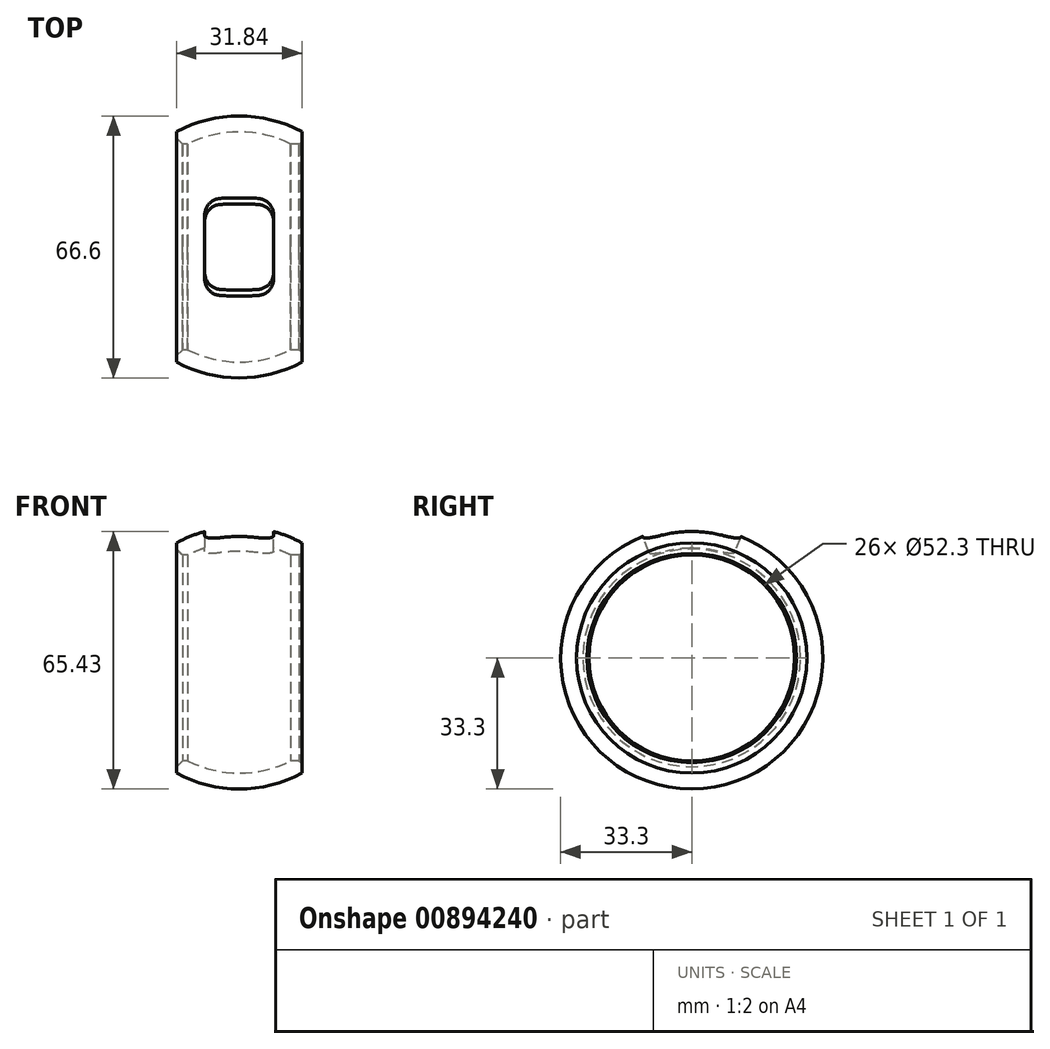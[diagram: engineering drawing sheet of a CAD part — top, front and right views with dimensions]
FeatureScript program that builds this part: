
annotation { "Feature Type Name" : "Feature", "Feature Type Description" : "" }
export const myFeature = defineFeature(function(context is Context, id is Id, definition is map)
    precondition{}
    {
        {
            var Q0;
            Q0=qCreatedBy(makeId("Front.planeOp"),FACE);
            var sketch = newSketch(context, id + "F0", { "sketchPlane" : qUnion([Q0])});
            skLineSegment(sketch, "E0", {"start": v(-15.92, 27.65) * mm, "end": v(-15.92, 29.25) * mm});
            skArc(sketch, "E1", {"start": v(15.92, 29.25) * mm, "mid": v(0, 33.3) * mm, "end": v(-15.92, 29.25) * mm});
            skLineSegment(sketch, "E2", {"start": v(15.22, 26.15) * mm, "end": v(13.07, 26.15) * mm});
            skLineSegment(sketch, "E3", {"start": v(-15.92, 27.65) * mm, "end": v(-14.42, 26.15) * mm});
            skLineSegment(sketch, "E4", {"start": v(-14.42, 26.15) * mm, "end": v(-13.07, 26.15) * mm});
            skLineSegment(sketch, "E5", {"start": v(15.92, 29.25) * mm, "end": v(15.92, 26.6) * mm});
            skLineSegment(sketch, "E6", {"start": v(15.92, 26.6) * mm, "end": v(15.22, 26.15) * mm});
            skArc(sketch, "E7", {"start": v(13.07, 26.15) * mm, "mid": v(0, 29.23) * mm, "end": v(-13.07, 26.15) * mm});
            skLineSegment(sketch, "E8", {"start": v(-15.92, 0) * mm, "end": v(15.92, 0) * mm, "construction": true});
            skSolve(sketch);
        }
        {
            var Q0;
            Q0=makeQuery(id+"F0.imprint","IMPRINT",FACE,{"disambiguationData":[TD([[makeQuery(id+"F0.imprint","IMPRINT",EDGE,{"derivedFrom":sQuery(id+"F0.wireOp",EDGE,"E0")}),-1.0]])]});
            var Q1;
            Q1=sQuery(id+"F0.wireOp",EDGE,"E8");
            revolve(context, id + "F1", {"surfaceOperationType" : NewSurfaceOperationType.NEW, "entities" : qUnion([Q0]), "axis" : qUnion([Q1]), "revolveType" : RevolveType.FULL});
        }
        {
            var Q0;
            Q0=qCreatedBy(makeId("Right.planeOp"),FACE);
            var sketch = newSketch(context, id + "F2", { "sketchPlane" : qUnion([Q0])});
            skLineSegment(sketch, "E9", {"start": v(-9.7, 24) * mm, "end": v(-13.74, 34) * mm});
            skLineSegment(sketch, "E10", {"start": v(-13.74, 34) * mm, "end": v(13.74, 34) * mm});
            skLineSegment(sketch, "E11", {"start": v(13.74, 34) * mm, "end": v(9.7, 24) * mm});
            skLineSegment(sketch, "E12", {"start": v(-9.7, 24) * mm, "end": v(0, 24) * mm});
            skLineSegment(sketch, "E13", {"start": v(0, 24) * mm, "end": v(9.7, 24) * mm});
            skLineSegment(sketch, "E14", {"start": v(0, 0) * mm, "end": v(9.7, 24) * mm, "construction": true});
            skSolve(sketch);
        }
        {
            var Q0;
            Q0=makeQuery(id+"F2.imprint","IMPRINT",FACE,{"disambiguationData":[TD([[makeQuery(id+"F2.imprint","IMPRINT",EDGE,{"derivedFrom":sQuery(id+"F2.wireOp",EDGE,"E9")}),-1.0]])]});
            extrude(context, id + "F3", {"entities" : qUnion([Q0]), "operationType" : NewBodyOperationType.REMOVE, "oppositeDirection" : true, "depth" : 17.5 * mm, "offsetDistance" : 25 * mm, "hasDraft" : true, "draftAngle" : 0 * degree, "symmetric" : true});
        }
        {
            var Q0;
            Q0=makeQuery(id+"F3.boolean.opBoolean","COPY",EDGE,{"derivedFrom":makeQuery(id+"F3.opExtrude","CAP_EDGE",EDGE,{"disambiguationData":[OSD([sQuery(id+"F2.wireOp",EDGE,"E9")])],"isStart":false})});
            var Q1;
            Q1=makeQuery(id+"F3.boolean.opBoolean","COPY",EDGE,{"derivedFrom":makeQuery(id+"F3.opExtrude","CAP_EDGE",EDGE,{"disambiguationData":[OSD([sQuery(id+"F2.wireOp",EDGE,"E9")])],"isStart":true})});
            var Q2;
            Q2=makeQuery(id+"F3.boolean.opBoolean","COPY",EDGE,{"derivedFrom":makeQuery(id+"F3.opExtrude","CAP_EDGE",EDGE,{"disambiguationData":[OSD([sQuery(id+"F2.wireOp",EDGE,"E11")])],"isStart":true})});
            var Q3;
            Q3=makeQuery(id+"F3.boolean.opBoolean","COPY",EDGE,{"derivedFrom":makeQuery(id+"F3.opExtrude","CAP_EDGE",EDGE,{"disambiguationData":[OSD([sQuery(id+"F2.wireOp",EDGE,"E11")])],"isStart":false})});
            fillet(context, id + "F4", {"entities" : qUnion([Q0, Q1, Q2, Q3]), "radius" : 4 * mm, "allowEdgeOverflow" : false});
        }
    });
